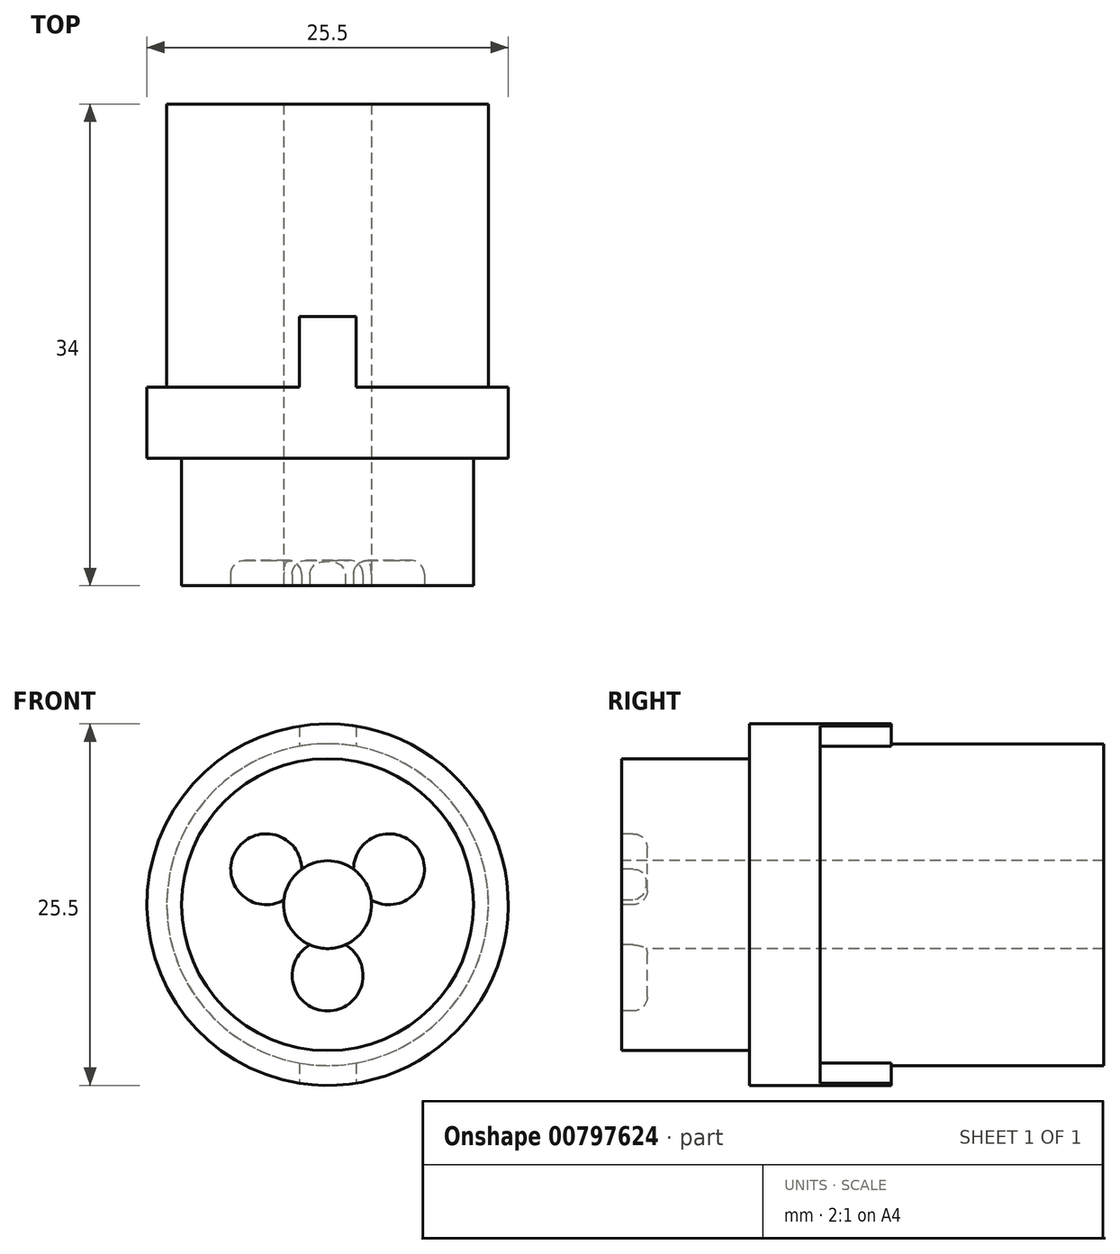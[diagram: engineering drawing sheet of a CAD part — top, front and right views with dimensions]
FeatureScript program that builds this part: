
annotation { "Feature Type Name" : "Feature", "Feature Type Description" : "" }
export const myFeature = defineFeature(function(context is Context, id is Id, definition is map)
    precondition{}
    {
        {
            var Q0;
            Q0=qCreatedBy(makeId("Front.planeOp"),FACE);
            var sketch = newSketch(context, id + "F0", { "sketchPlane" : qUnion([Q0])});
            skCircle(sketch, "E0", {"center": v(0, 0) * mm, "radius": 10.3 * mm});
            skSolve(sketch);
        }
        {
            var Q0;
            Q0=makeQuery(id+"F0.imprint","IMPRINT",FACE,{"disambiguationData":[TD([[makeQuery(id+"F0.imprint","IMPRINT",EDGE,{"derivedFrom":sQuery(id+"F0.wireOp",EDGE,"E0")}),1.0]])]});
            extrude(context, id + "F1", {"entities" : qUnion([Q0]), "depth" : 9 * mm, "offsetDistance" : 25 * mm});
        }
        {
            var Q0;
            Q0=makeQuery(id+"F1.opExtrude","CAP_FACE",FACE,{"disambiguationData":[OSD([sQuery(id+"F0.wireOp",EDGE,"E0")])],"isStart":true});
            var sketch = newSketch(context, id + "F2", { "sketchPlane" : qUnion([Q0])});
            skCircle(sketch, "E1", {"center": v(0, 0) * mm, "radius": 9.25 * mm});
            skCircle(sketch, "E2", {"center": v(0, 0) * mm, "radius": 11.25 * mm});
            skSolve(sketch);
        }
        {
            var Q0;
            Q0=makeQuery(id+"F1.opExtrude","CAP_FACE",FACE,{"disambiguationData":[OSD([sQuery(id+"F0.wireOp",EDGE,"E0")])],"isStart":false});
            var sketch = newSketch(context, id + "F3", { "sketchPlane" : qUnion([Q0])});
            skCircle(sketch, "E3", {"center": v(0, 0) * mm, "radius": 3.1 * mm});
            skSolve(sketch);
        }
        {
            var Q0;
            Q0=makeQuery(id+"F3.imprint","IMPRINT",FACE,{"disambiguationData":[TD([[makeQuery(id+"F3.imprint","IMPRINT",EDGE,{"derivedFrom":sQuery(id+"F3.wireOp",EDGE,"E3")}),1.0]])]});
            extrude(context, id + "F4", {"entities" : qUnion([Q0]), "operationType" : NewBodyOperationType.REMOVE, "endBound" : BoundingType.THROUGH_ALL, "oppositeDirection" : true, "depth" : 25 * mm, "offsetDistance" : 25 * mm});
        }
        {
            var Q0;
            Q0=makeQuery(id+"F1.opExtrude","CAP_FACE",FACE,{"disambiguationData":[OSD([sQuery(id+"F0.wireOp",EDGE,"E0")])],"isStart":false});
            var sketch = newSketch(context, id + "F5", { "sketchPlane" : qUnion([Q0])});
            skCircle(sketch, "E4", {"center": v(-4.33, 2.5) * mm, "radius": 2.5 * mm});
            skCircle(sketch, "E5", {"center": v(4.33, 2.5) * mm, "radius": 2.5 * mm});
            skCircle(sketch, "E6", {"center": v(0, -5) * mm, "radius": 2.5 * mm});
            skSolve(sketch);
        }
        {
            var Q0;
            {var subQ0=sQuery(id+"F5.wireOp",EDGE,"E4");var subQ1=makeQuery(id+"F4.boolean.opBoolean","COPY",EDGE,{"derivedFrom":makeQuery(id+"F4.opExtrude","CAP_EDGE",EDGE,{"disambiguationData":[OSD([sQuery(id+"F3.wireOp",EDGE,"E3")])],"isStart":true})});var subQ2=makeQuery(id+"F5.imprint","INTERSECT",VERTEX,{"disambiguationData":[OD(0.0)],"derivedFrom":[subQ1,subQ0]});Q0=makeQuery(id+"F5.imprint","IMPRINT",FACE,{"disambiguationData":[TD([[makeQuery(id+"F5.imprint","IMPRINT",EDGE,{"disambiguationData":[TD([[subQ2,1.0]])],"derivedFrom":subQ0}),1.0]])]});}
            var Q1;
            {var subQ0=sQuery(id+"F5.wireOp",EDGE,"E5");var subQ1=makeQuery(id+"F4.boolean.opBoolean","COPY",EDGE,{"derivedFrom":makeQuery(id+"F4.opExtrude","CAP_EDGE",EDGE,{"disambiguationData":[OSD([sQuery(id+"F3.wireOp",EDGE,"E3")])],"isStart":true})});var subQ2=makeQuery(id+"F5.imprint","INTERSECT",VERTEX,{"disambiguationData":[OD(0.0)],"derivedFrom":[subQ1,subQ0]});Q1=makeQuery(id+"F5.imprint","IMPRINT",FACE,{"disambiguationData":[TD([[makeQuery(id+"F5.imprint","IMPRINT",EDGE,{"disambiguationData":[TD([[subQ2,1.0]])],"derivedFrom":subQ0}),1.0]])]});}
            var Q2;
            {var subQ0=sQuery(id+"F5.wireOp",EDGE,"E6");var subQ1=makeQuery(id+"F4.boolean.opBoolean","COPY",EDGE,{"derivedFrom":makeQuery(id+"F4.opExtrude","CAP_EDGE",EDGE,{"disambiguationData":[OSD([sQuery(id+"F3.wireOp",EDGE,"E3")])],"isStart":true})});var subQ2=makeQuery(id+"F5.imprint","INTERSECT",VERTEX,{"disambiguationData":[OD(0.0)],"derivedFrom":[subQ1,subQ0]});Q2=makeQuery(id+"F5.imprint","IMPRINT",FACE,{"disambiguationData":[TD([[makeQuery(id+"F5.imprint","IMPRINT",EDGE,{"disambiguationData":[TD([[subQ2,-1.0]])],"derivedFrom":subQ0}),1.0]])]});}
            extrude(context, id + "F6", {"entities" : qUnion([Q0, Q1, Q2]), "operationType" : NewBodyOperationType.REMOVE, "oppositeDirection" : true, "depth" : 1.8 * mm, "offsetDistance" : 25 * mm});
        }
        {
            var Q0;
            Q0=makeQuery(id+"F6.boolean.opBoolean","COPY",EDGE,{"derivedFrom":makeQuery(id+"F6.opExtrude","CAP_EDGE",EDGE,{"disambiguationData":[OSD([sQuery(id+"F5.wireOp",EDGE,"E4")])],"isStart":false})});
            var Q1;
            Q1=makeQuery(id+"F6.boolean.opBoolean","COPY",EDGE,{"derivedFrom":makeQuery(id+"F6.opExtrude","CAP_EDGE",EDGE,{"disambiguationData":[OSD([sQuery(id+"F5.wireOp",EDGE,"E5")])],"isStart":false})});
            var Q2;
            Q2=makeQuery(id+"F6.boolean.opBoolean","COPY",EDGE,{"derivedFrom":makeQuery(id+"F6.opExtrude","CAP_EDGE",EDGE,{"disambiguationData":[OSD([sQuery(id+"F5.wireOp",EDGE,"E6")])],"isStart":false})});
            fillet(context, id + "F7", {"entities" : qUnion([Q0, Q1, Q2]), "radius" : 1 * mm, "tangentPropagation" : true, "allowEdgeOverflow" : false});
        }
        {
            var Q0;
            Q0=makeQuery(id+"F2.imprint","IMPRINT",FACE,{"disambiguationData":[TD([[makeQuery(id+"F2.imprint","IMPRINT",EDGE,{"derivedFrom":sQuery(id+"F2.wireOp",EDGE,"E1")}),1.0]])]});
            cPlane(context, id + "F8", {"entities" : qUnion([Q0]), "cplaneType" : CPlaneType.OFFSET, "offset" : 0 * mm, "width" : 150 * mm, "height" : 150 * mm});
        }
        {
            var Q0;
            Q0=qCreatedBy(id+"F8.planeOp",FACE);
            var sketch = newSketch(context, id + "F9", { "sketchPlane" : qUnion([Q0])});
            skCircle(sketch, "E7", {"center": v(0, 0) * mm, "radius": 12.75 * mm});
            skSolve(sketch);
        }
        {
            var Q0;
            Q0 = qSketchRegion(id + "F9", true);
            extrude(context, id + "F10", {"entities" : qUnion([Q0]), "operationType" : NewBodyOperationType.ADD, "depth" : 25 * mm, "offsetDistance" : 25 * mm});
        }
        {
            var Q0;
            Q0=makeQuery(id+"F10.opExtrude","CAP_FACE",FACE,{"disambiguationData":[OSD([sQuery(id+"F9.wireOp",EDGE,"E7")])],"isStart":false});
            var sketch = newSketch(context, id + "F11", { "sketchPlane" : qUnion([Q0])});
            skCircle(sketch, "E8", {"center": v(0, 0) * mm, "radius": 3.1 * mm});
            skSolve(sketch);
        }
        {
            var Q0;
            Q0=makeQuery(id+"F11.imprint","IMPRINT",FACE,{"disambiguationData":[TD([[makeQuery(id+"F11.imprint","IMPRINT",EDGE,{"derivedFrom":sQuery(id+"F11.wireOp",EDGE,"E8")}),1.0]])]});
            extrude(context, id + "F12", {"entities" : qUnion([Q0]), "operationType" : NewBodyOperationType.REMOVE, "endBound" : BoundingType.THROUGH_ALL, "oppositeDirection" : true, "depth" : 25 * mm, "offsetDistance" : 25 * mm});
        }
        {
            var Q0;
            Q0=makeQuery(id+"F10.opExtrude","CAP_FACE",FACE,{"disambiguationData":[OSD([sQuery(id+"F9.wireOp",EDGE,"E7")])],"isStart":false});
            var sketch = newSketch(context, id + "F13", { "sketchPlane" : qUnion([Q0])});
            skCircle(sketch, "E9", {"center": v(0, 0) * mm, "radius": 11.35 * mm});
            skSolve(sketch);
        }
        {
            var Q0;
            Q0=makeQuery(id+"F13.imprint","IMPRINT",FACE,{"disambiguationData":[TD([[makeQuery(id+"F13.imprint","IMPRINT",EDGE,{"derivedFrom":sQuery(id+"F13.wireOp",EDGE,"E9")}),-1.0]])]});
            extrude(context, id + "F14", {"entities" : qUnion([Q0]), "operationType" : NewBodyOperationType.REMOVE, "oppositeDirection" : true, "depth" : 20 * mm, "offsetDistance" : 25 * mm});
        }
        {
            var Q0;
            Q0=makeQuery(id+"F14.boolean.opBoolean","COPY",FACE,{"derivedFrom":makeQuery(id+"F14.opExtrude","CAP_FACE",FACE,{"disambiguationData":[OSD([sQuery(id+"F9.wireOp",EDGE,"E7"),sQuery(id+"F13.wireOp",EDGE,"E9")])],"isStart":false})});
            var sketch = newSketch(context, id + "F15", { "sketchPlane" : qUnion([Q0])});
            skLineSegment(sketch, "E10", {"start": v(0, 13.66) * mm, "end": v(0, -14.8) * mm, "construction": true});
            skLineSegment(sketch, "E11", {"start": v(-2, 12.6) * mm, "end": v(-2, 11.17) * mm});
            skLineSegment(sketch, "E12", {"start": v(2, 12.6) * mm, "end": v(2, 11.17) * mm});
            skLineSegment(sketch, "E13", {"start": v(-14.5, 0) * mm, "end": v(13.95, 0) * mm, "construction": true});
            skLineSegment(sketch, "E14.MirrorCS", {"start": v(-6, 12.6) * mm, "end": v(-6, 11.17) * mm});
            skLineSegment(sketch, "E15.MirrorCS", {"start": v(10.5, 0) * mm, "end": v(-17.95, 0) * mm, "construction": true});
            skLineSegment(sketch, "E16", {"start": v(-2, -11.17) * mm, "end": v(-2, -12.6) * mm});
            skLineSegment(sketch, "E17", {"start": v(2, -11.17) * mm, "end": v(2, -12.6) * mm});
            skPoint(sketch, "E18.MirrorCS.end.orphan", {"position": v(-6, 11.17) * mm});
            skPoint(sketch, "E18.MirrorCS.start.orphan", {"position": v(-6, 12.6) * mm});
            skSolve(sketch);
        }
        {
            var Q0;
            {var subQ0=sQuery(id+"F15.wireOp",EDGE,"E11");Q0=makeQuery(id+"F15.imprint","IMPRINT",FACE,{"disambiguationData":[TD([[makeQuery(id+"F15.imprint","IMPRINT",EDGE,{"derivedFrom":subQ0}),1.0]])]});}
            var Q1;
            {var subQ0=sQuery(id+"F15.wireOp",EDGE,"E16");Q1=makeQuery(id+"F15.imprint","IMPRINT",FACE,{"disambiguationData":[TD([[makeQuery(id+"F15.imprint","IMPRINT",EDGE,{"derivedFrom":subQ0}),1.0]])]});}
            extrude(context, id + "F16", {"entities" : qUnion([Q0, Q1]), "operationType" : NewBodyOperationType.ADD, "depth" : 5 * mm, "offsetDistance" : 25 * mm});
        }
    });
